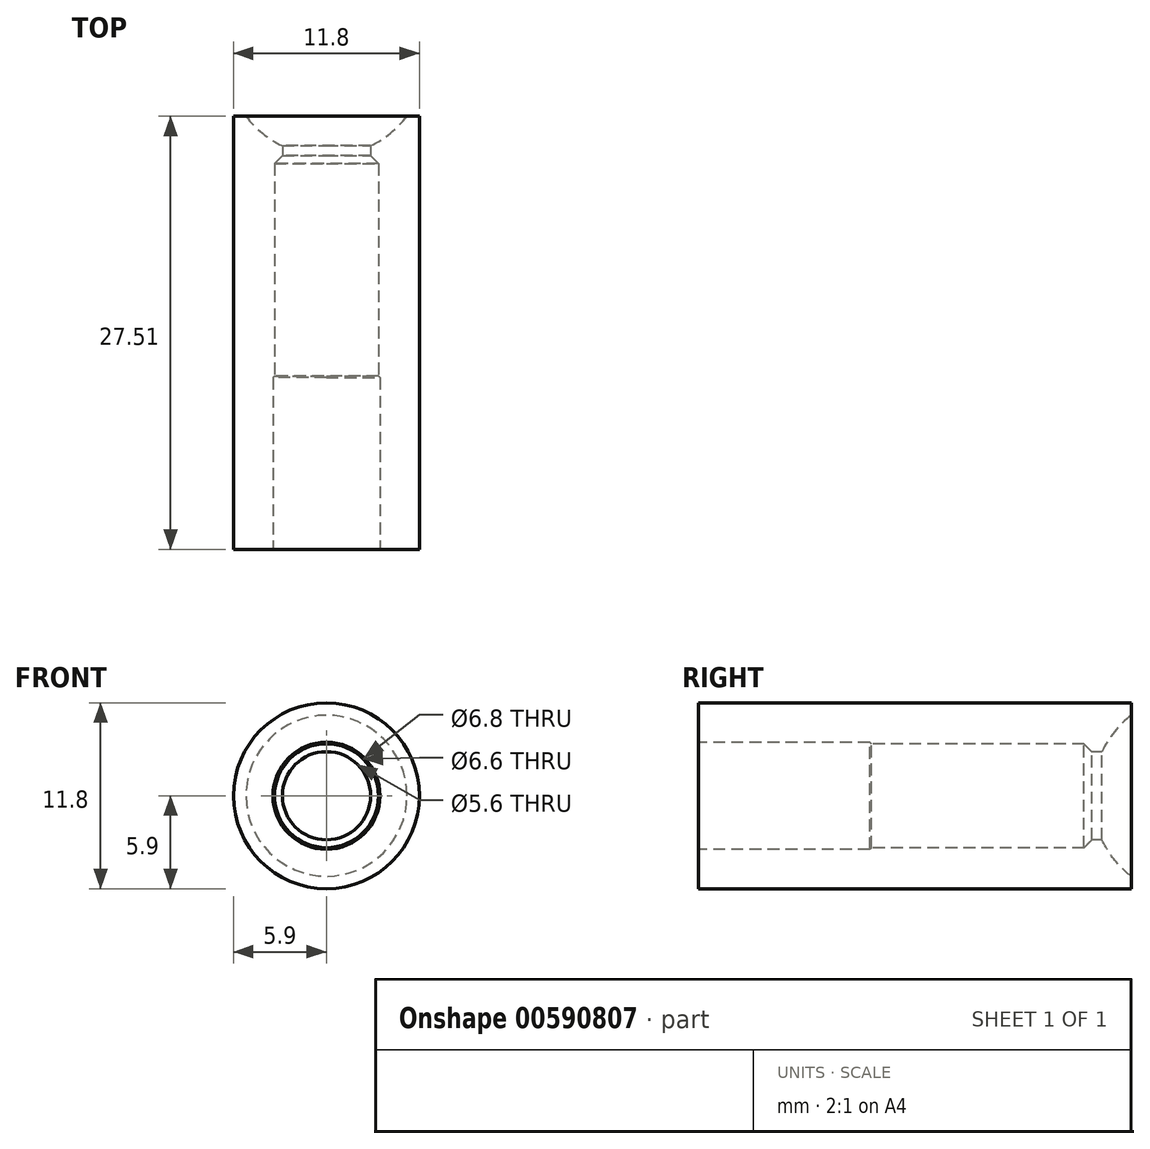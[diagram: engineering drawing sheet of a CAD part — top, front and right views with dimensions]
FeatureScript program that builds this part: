
annotation { "Feature Type Name" : "Feature", "Feature Type Description" : "" }
export const myFeature = defineFeature(function(context is Context, id is Id, definition is map)
    precondition{}
    {
        {
            var Q0;
            Q0=qCreatedBy(makeId("Right.planeOp"),FACE);
            var sketch = newSketch(context, id + "F0", { "sketchPlane" : qUnion([Q0])});
            skCircle(sketch, "E0", {"center": v(13.4, 0) * mm, "radius": 6.47 * mm});
            skLineSegment(sketch, "E1.bottom", {"start": v(6.42, 3.3) * mm, "end": v(-6.43, 3.3) * mm});
            skLineSegment(sketch, "E1.top", {"start": v(6.43, -3.3) * mm, "end": v(-6.43, -3.3) * mm});
            skLineSegment(sketch, "E1.left", {"start": v(6.42, 3.3) * mm, "end": v(6.43, -3.3) * mm});
            skLineSegment(sketch, "E1.right", {"start": v(-6.43, 3.3) * mm, "end": v(-6.43, -3.3) * mm});
            skPoint(sketch, "E1.middle", {"position": v(0, 0) * mm});
            skLineSegment(sketch, "E2.bottom", {"start": v(-7.08, 3.4) * mm, "end": v(-18.07, 3.4) * mm});
            skLineSegment(sketch, "E2.top", {"start": v(-7.08, -3.4) * mm, "end": v(-18.07, -3.4) * mm});
            skLineSegment(sketch, "E2.left", {"start": v(-7.08, 3.4) * mm, "end": v(-7.08, -3.4) * mm});
            skLineSegment(sketch, "E2.right", {"start": v(-18.07, 3.4) * mm, "end": v(-18.07, -3.4) * mm});
            skPoint(sketch, "E2.middle", {"position": v(-12.58, 0) * mm});
            skLineSegment(sketch, "E3", {"start": v(0, 0) * mm, "end": v(2.43, 0) * mm, "construction": true});
            skLineSegment(sketch, "E4", {"start": v(6.42, 1.5) * mm, "end": v(7.1, 1.5) * mm});
            skLineSegment(sketch, "E5", {"start": v(-18.07, 3.4) * mm, "end": v(-18.07, 5.9) * mm});
            skLineSegment(sketch, "E6", {"start": v(-18.07, 5.9) * mm, "end": v(10.73, 5.9) * mm});
            skLineSegment(sketch, "E7", {"start": v(-6.43, 3.3) * mm, "end": v(-7.08, 3.3) * mm});
            skLineSegment(sketch, "E8", {"start": v(9.42, 5.9) * mm, "end": v(9.42, 5.11) * mm});
            skLineSegment(sketch, "E9", {"start": v(6.93, 3.3) * mm, "end": v(6.93, 0) * mm});
            skLineSegment(sketch, "E10", {"start": v(6.42, 3.3) * mm, "end": v(6.93, 3.3) * mm});
            skLineSegment(sketch, "E11", {"start": v(6.42, 3.3) * mm, "end": v(6.93, 2.8) * mm});
            skLineSegment(sketch, "E12", {"start": v(6.93, 2.8) * mm, "end": v(7.56, 2.8) * mm});
            skSolve(sketch);
        }
        {
            var Q0;
            Q0=makeQuery(id+"F0.imprint","IMPRINT",FACE,{"disambiguationData":[TD([[makeQuery(id+"F0.imprint","IMPRINT",EDGE,{"derivedFrom":sQuery(id+"F0.wireOp",EDGE,"E1.bottom")}),-1.0]])]});
            var Q1;
            {var subQ0=sQuery(id+"F0.wireOp",EDGE,"E10");Q1=makeQuery(id+"F0.imprint","IMPRINT",FACE,{"disambiguationData":[TD([[makeQuery(id+"F0.imprint","IMPRINT",EDGE,{"derivedFrom":subQ0}),-1.0]])]});}
            var Q2;
            Q2=sQuery(id+"F0.wireOp",EDGE,"E3");
            revolve(context, id + "F1", {"entities" : qUnion([Q0, Q1]), "axis" : qUnion([Q2]), "revolveType" : RevolveType.FULL});
        }
        {
            var Q0;
            Q0=makeQuery(id+"F1.opRevolve","SWEPT_EDGE",EDGE,{"disambiguationData":[OSD([sQuery(id+"F0.wireOp",EDGE,"E2.bottom"),sQuery(id+"F0.wireOp",EDGE,"E2.left")])]});
            chamfer(context, id + "F2", {"entities" : qUnion([Q0]), "width" : .1 * mm, "tangentPropagation" : true});
        }
    });
